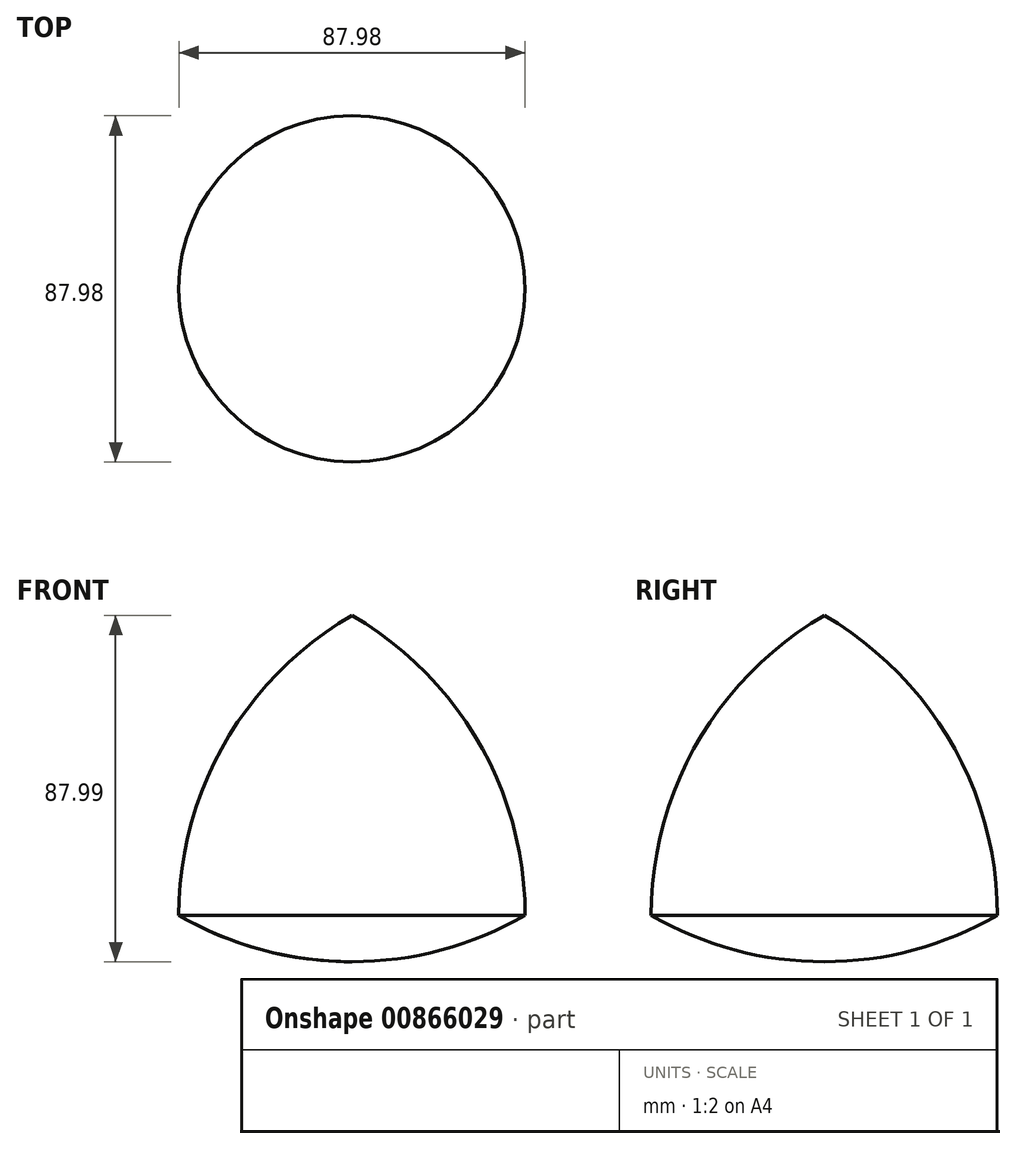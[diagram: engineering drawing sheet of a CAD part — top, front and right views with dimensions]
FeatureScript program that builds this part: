
annotation { "Feature Type Name" : "Feature", "Feature Type Description" : "" }
export const myFeature = defineFeature(function(context is Context, id is Id, definition is map)
    precondition{}
    {
        {
            var Q0;
            Q0=qCreatedBy(makeId("Front.planeOp"),FACE);
            var sketch = newSketch(context, id + "F0", { "sketchPlane" : qUnion([Q0])});
            skLineSegment(sketch, "E0", {"start": v(-44, -25.4) * mm, "end": v(0, 50.8) * mm});
            skLineSegment(sketch, "E1", {"start": v(0, -25.4) * mm, "end": v(-44, -25.4) * mm});
            skArc(sketch, "E2", {"start": v(-44, -25.4) * mm, "mid": v(-22.77, -34.2) * mm, "end": v(0, -37.19) * mm});
            skArc(sketch, "E3.trimOffspring", {"start": v(0, 50.8) * mm, "mid": v(-32.2, 18.6) * mm, "end": v(-44, -25.4) * mm});
            skLineSegment(sketch, "E4", {"start": v(0, 50.8) * mm, "end": v(0, -37.19) * mm});
            skSolve(sketch);
        }
        {
            var Q0;
            Q0=makeQuery(id+"F0.imprint","IMPRINT",FACE,{"disambiguationData":[TD([[makeQuery(id+"F0.imprint","IMPRINT",EDGE,{"derivedFrom":sQuery(id+"F0.wireOp",EDGE,"E0")}),1.0]])]});
            var Q1;
            {var subQ0=sQuery(id+"F0.wireOp",EDGE,"E0");Q1=makeQuery(id+"F0.imprint","IMPRINT",FACE,{"disambiguationData":[TD([[makeQuery(id+"F0.imprint","IMPRINT",EDGE,{"derivedFrom":subQ0}),-1.0]])]});}
            var Q2;
            {var subQ0=sQuery(id+"F0.wireOp",EDGE,"E1");Q2=makeQuery(id+"F0.imprint","IMPRINT",FACE,{"disambiguationData":[TD([[makeQuery(id+"F0.imprint","IMPRINT",EDGE,{"derivedFrom":subQ0}),1.0]])]});}
            var Q3;
            Q3=sQuery(id+"F0.wireOp",EDGE,"E4");
            revolve(context, id + "F1", {"surfaceOperationType" : NewSurfaceOperationType.NEW, "entities" : qUnion([Q0, Q1, Q2]), "axis" : qUnion([Q3]), "revolveType" : RevolveType.FULL});
        }
    });
